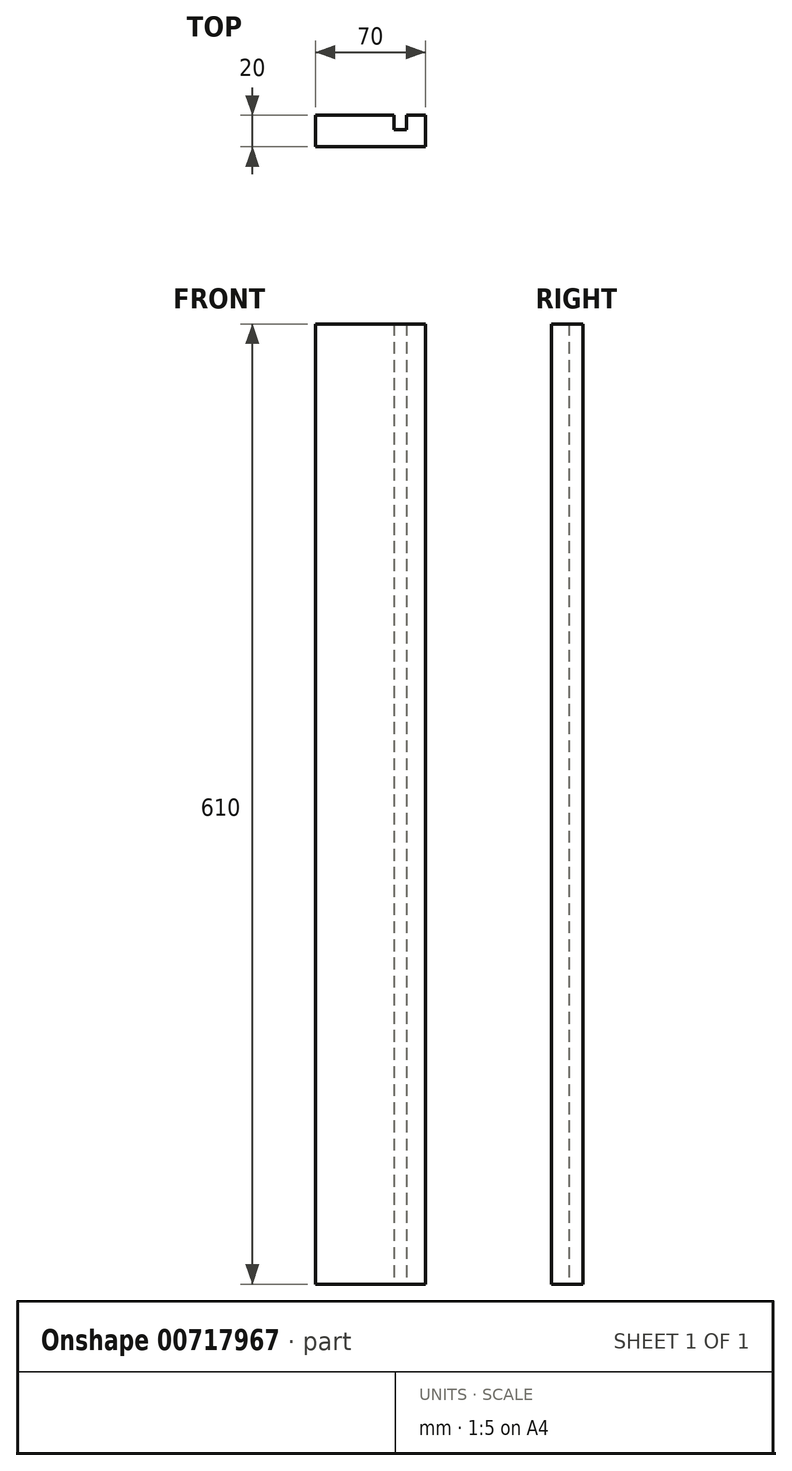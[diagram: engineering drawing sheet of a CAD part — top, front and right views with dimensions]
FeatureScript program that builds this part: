
annotation { "Feature Type Name" : "Feature", "Feature Type Description" : "" }
export const myFeature = defineFeature(function(context is Context, id is Id, definition is map)
    precondition{}
    {
        {
            var Q0;
            Q0=qCreatedBy(makeId("Front.planeOp"),FACE);
            var sketch = newSketch(context, id + "F0", { "sketchPlane" : qUnion([Q0])});
            skLineSegment(sketch, "E0.bottom", {"start": v(-93.13, 384.72) * mm, "end": v(-23.13, 384.72) * mm});
            skLineSegment(sketch, "E0.top", {"start": v(-93.13, -225.28) * mm, "end": v(-23.13, -225.28) * mm});
            skLineSegment(sketch, "E0.left", {"start": v(-93.13, 384.72) * mm, "end": v(-93.13, -225.28) * mm});
            skLineSegment(sketch, "E0.right", {"start": v(-23.13, 384.72) * mm, "end": v(-23.13, -225.28) * mm});
            skSolve(sketch);
        }
        {
            var Q0;
            Q0=qSketchRegion(id+"F0",true);
            extrude(context, id + "F1", {"entities" : qUnion([Q0]), "oppositeDirection" : true, "depth" : 20 * mm, "offsetDistance" : 25.4 * mm});
        }
        {
            var Q0;
            Q0=makeQuery(id+"F1.opExtrude","CAP_FACE",FACE,{"disambiguationData":[OSD([sQuery(id+"F0.wireOp",EDGE,"E0.bottom"),sQuery(id+"F0.wireOp",EDGE,"E0.top"),sQuery(id+"F0.wireOp",EDGE,"E0.left"),sQuery(id+"F0.wireOp",EDGE,"E0.right")])],"isStart":false});
            var sketch = newSketch(context, id + "F2", { "sketchPlane" : qUnion([Q0])});
            skLineSegment(sketch, "E1.bottom", {"start": v(35.13, 384.72) * mm, "end": v(43.13, 384.72) * mm});
            skLineSegment(sketch, "E1.top", {"start": v(35.13, -1115.28) * mm, "end": v(43.13, -1115.28) * mm});
            skLineSegment(sketch, "E1.left", {"start": v(35.13, 384.72) * mm, "end": v(35.13, -1115.28) * mm});
            skLineSegment(sketch, "E1.right", {"start": v(43.13, 384.72) * mm, "end": v(43.13, -1115.28) * mm});
            skSolve(sketch);
        }
        {
            var Q0;
            Q0=makeQuery(id+"F2.imprint","IMPRINT",FACE,{"disambiguationData":[TD([[makeQuery(id+"F2.imprint","IMPRINT",EDGE,{"derivedFrom":sQuery(id+"F2.wireOp",EDGE,"E1.bottom")}),1.0]])]});
            extrude(context, id + "F3", {"entities" : qUnion([Q0]), "operationType" : NewBodyOperationType.REMOVE, "oppositeDirection" : true, "depth" : 9 * mm, "offsetDistance" : 25.4 * mm});
        }
    });
